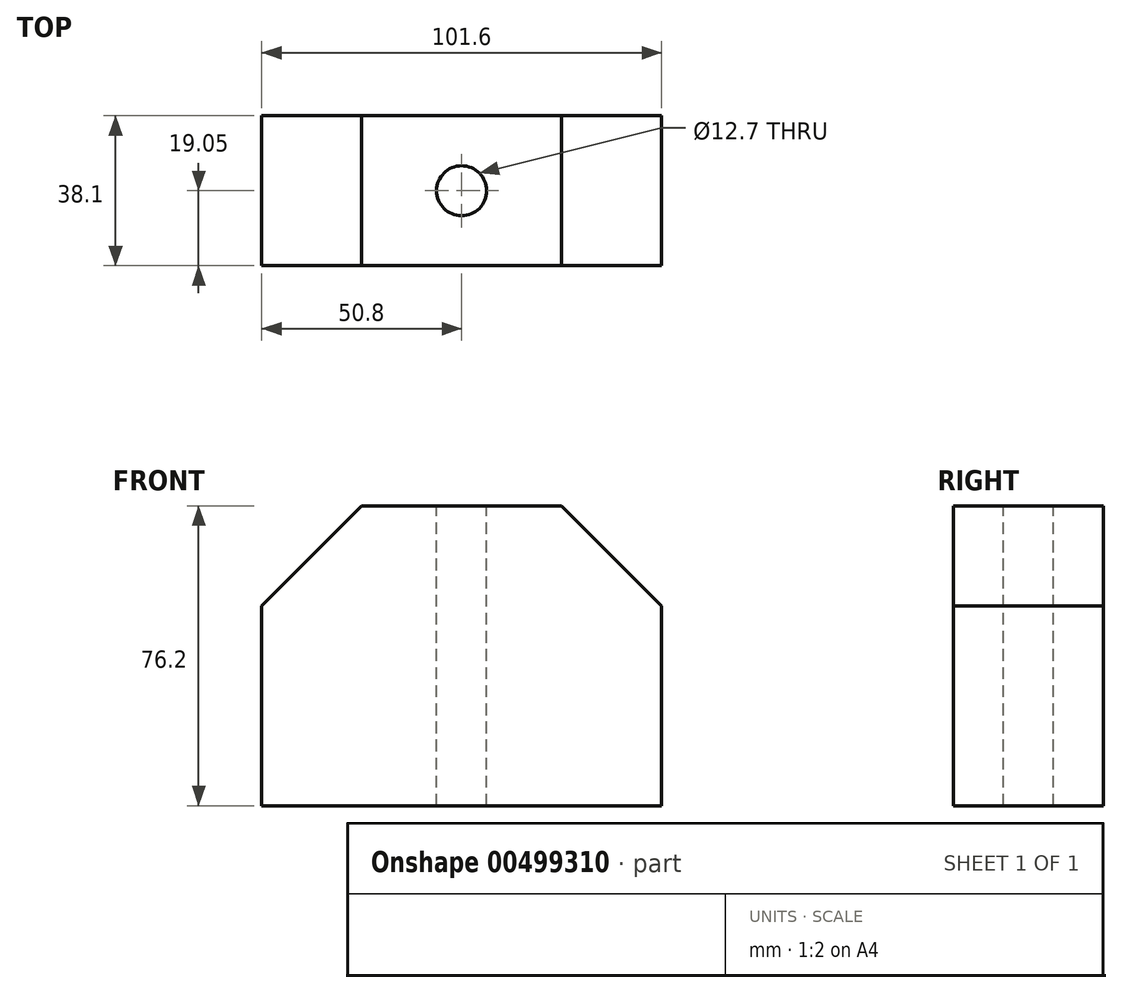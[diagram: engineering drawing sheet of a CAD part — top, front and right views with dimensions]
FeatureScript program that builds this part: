
annotation { "Feature Type Name" : "Feature", "Feature Type Description" : "" }
export const myFeature = defineFeature(function(context is Context, id is Id, definition is map)
    precondition{}
    {
        {
            var Q0;
            Q0=qCreatedBy(makeId("Front.planeOp"),FACE);
            var sketch = newSketch(context, id + "F0", { "sketchPlane" : qUnion([Q0])});
            skLineSegment(sketch, "E0", {"start": v(0, 0) * mm, "end": v(101.6, 0) * mm});
            skLineSegment(sketch, "E1", {"start": v(101.6, 0) * mm, "end": v(101.6, 50.8) * mm});
            skLineSegment(sketch, "E2", {"start": v(101.6, 50.8) * mm, "end": v(76.2, 76.2) * mm});
            skLineSegment(sketch, "E3", {"start": v(76.2, 76.2) * mm, "end": v(25.4, 76.2) * mm});
            skLineSegment(sketch, "E4", {"start": v(25.4, 76.2) * mm, "end": v(0, 50.8) * mm});
            skLineSegment(sketch, "E5", {"start": v(0, 50.8) * mm, "end": v(0, 0) * mm});
            skSolve(sketch);
        }
        {
            var Q0;
            Q0=makeQuery(id+"F0.imprint","IMPRINT",FACE,{"disambiguationData":[TD([[makeQuery(id+"F0.imprint","IMPRINT",EDGE,{"derivedFrom":sQuery(id+"F0.wireOp",EDGE,"E0")}),1.0]])]});
            extrude(context, id + "F1", {"entities" : qUnion([Q0]), "depth" : 38.1 * mm});
        }
        {
            var Q0;
            Q0=makeQuery(id+"F1.opExtrude","SWEPT_FACE",FACE,{"disambiguationData":[OSD([sQuery(id+"F0.wireOp",EDGE,"E3")])]});
            var sketch = newSketch(context, id + "F2", { "sketchPlane" : qUnion([Q0])});
            skPoint(sketch, "E6.endSnap0", {"position": v(76.2, -19.05) * mm});
            skLineSegment(sketch, "E7", {"start": v(50.8, -38.1) * mm, "end": v(50.8, -19.05) * mm});
            skPoint(sketch, "E7.endSnap0", {"position": v(25.4, -19.05) * mm});
            skCircle(sketch, "E8", {"center": v(50.8, -19.05) * mm, "radius": 6.35 * mm});
            skSolve(sketch);
        }
        {
            var Q0;
            Q0=makeQuery(id+"F2.imprint","IMPRINT",FACE,{"disambiguationData":[TD([[makeQuery(id+"F2.imprint","IMPRINT",EDGE,{"derivedFrom":sQuery(id+"F2.wireOp",EDGE,"E8")}),1.0]])]});
            extrude(context, id + "F3", {"entities" : qUnion([Q0]), "operationType" : NewBodyOperationType.REMOVE, "endBound" : BoundingType.THROUGH_ALL, "oppositeDirection" : true, "depth" : 25.4 * mm});
        }
    });
